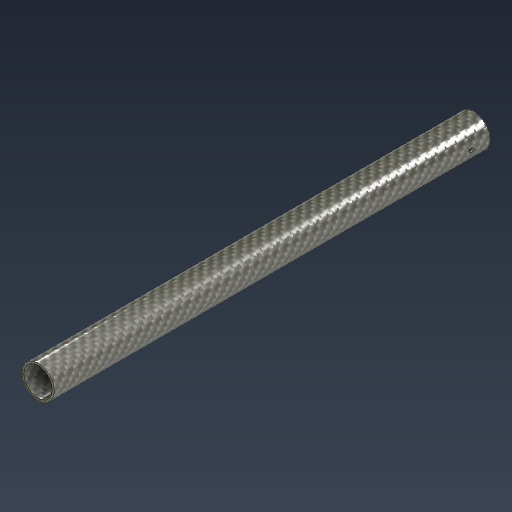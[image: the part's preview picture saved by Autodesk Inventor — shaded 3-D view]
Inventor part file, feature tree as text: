
AUTODESK INVENTOR PART (.ipt)
format: ipt  version: 2024.1 (Build 281209000, 209)  size: 161,792 bytes
history: native  units: mm
features: extrude x2, sketch x1
ambient origin geometry x8: Origin, YZ Plane, XZ Plane, XY Plane, X Axis, Y Axis, Z Axis, Center Point
bodies: Solid1 (feature_tree)
feature tree (3):
  extrude  "Extrusion1"  Depth=14.4mm
  extrude  "Extrusion3"  Depth=14.4mm TaperAngle=0.0deg
  sketch  "Sketch3"  dims[d0=25.0mm d1=22.0mm d2=335.7175mm d3=0.0mm d9=3.2mm d10=25.0mm d11=0.0mm d12=14.4mm]
